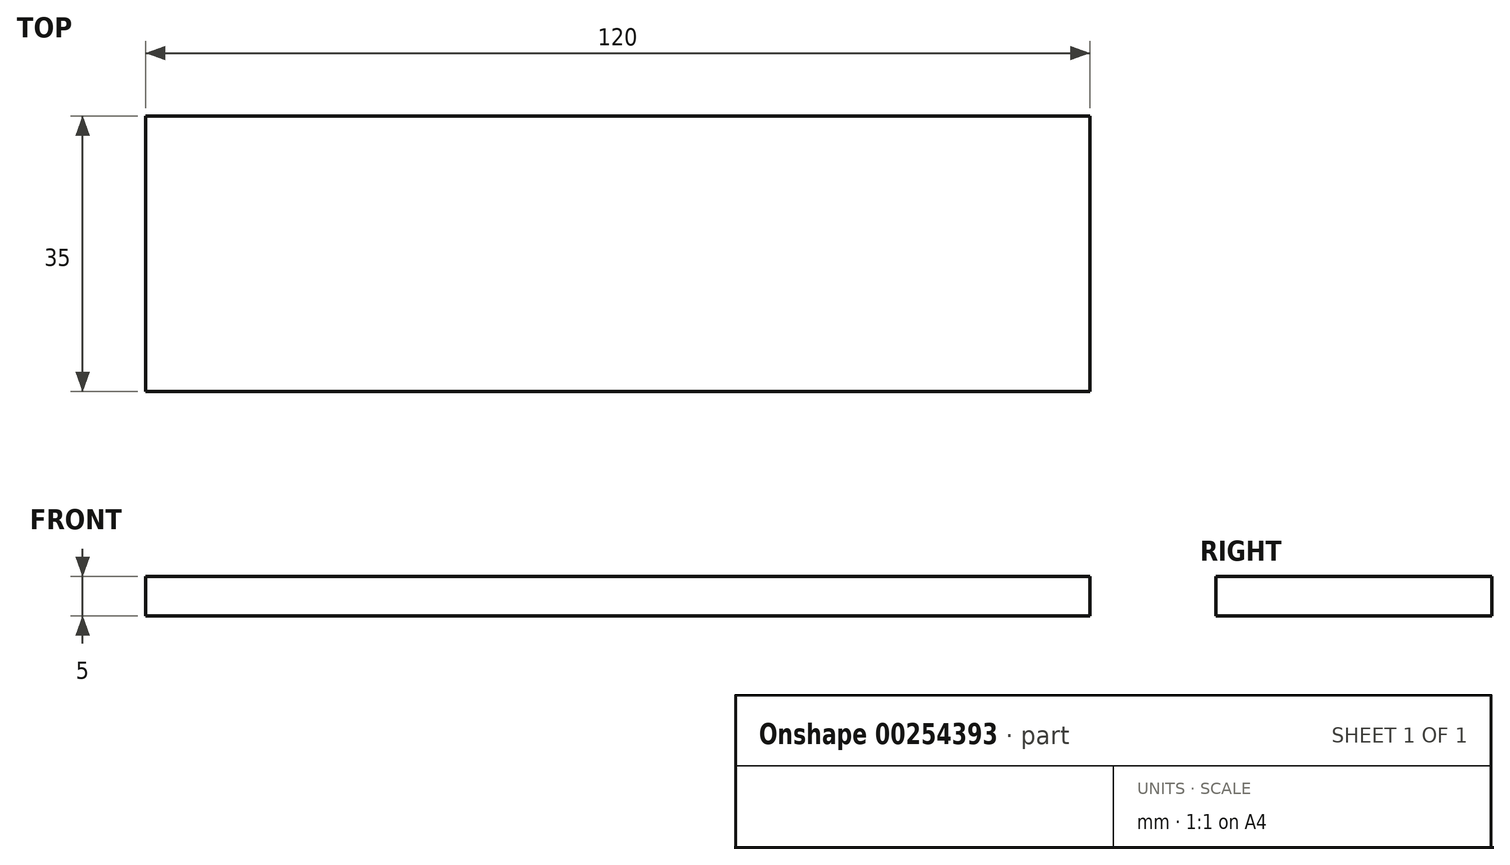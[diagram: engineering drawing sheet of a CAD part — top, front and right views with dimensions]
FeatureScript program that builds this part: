
annotation { "Feature Type Name" : "Feature", "Feature Type Description" : "" }
export const myFeature = defineFeature(function(context is Context, id is Id, definition is map)
    precondition{}
    {
        {
            var Q0;
            Q0=qCreatedBy(makeId("Top.planeOp"),FACE);
            var sketch = newSketch(context, id + "F0", { "sketchPlane" : qUnion([Q0])});
            skLineSegment(sketch, "E0.bottom", {"start": v(60, -17.5) * mm, "end": v(-60, -17.5) * mm});
            skLineSegment(sketch, "E0.top", {"start": v(60, 17.5) * mm, "end": v(-60, 17.5) * mm});
            skLineSegment(sketch, "E0.left", {"start": v(60, -17.5) * mm, "end": v(60, 17.5) * mm});
            skLineSegment(sketch, "E0.right", {"start": v(-60, -17.5) * mm, "end": v(-60, 17.5) * mm});
            skPoint(sketch, "E0.middle", {"position": v(0, 0) * mm});
            skSolve(sketch);
        }
        {
            var Q0;
            Q0 = qSketchRegion(id + "F0", true);
            extrude(context, id + "F1", {"entities" : qUnion([Q0]), "depth" : 5 * mm});
        }
    });
